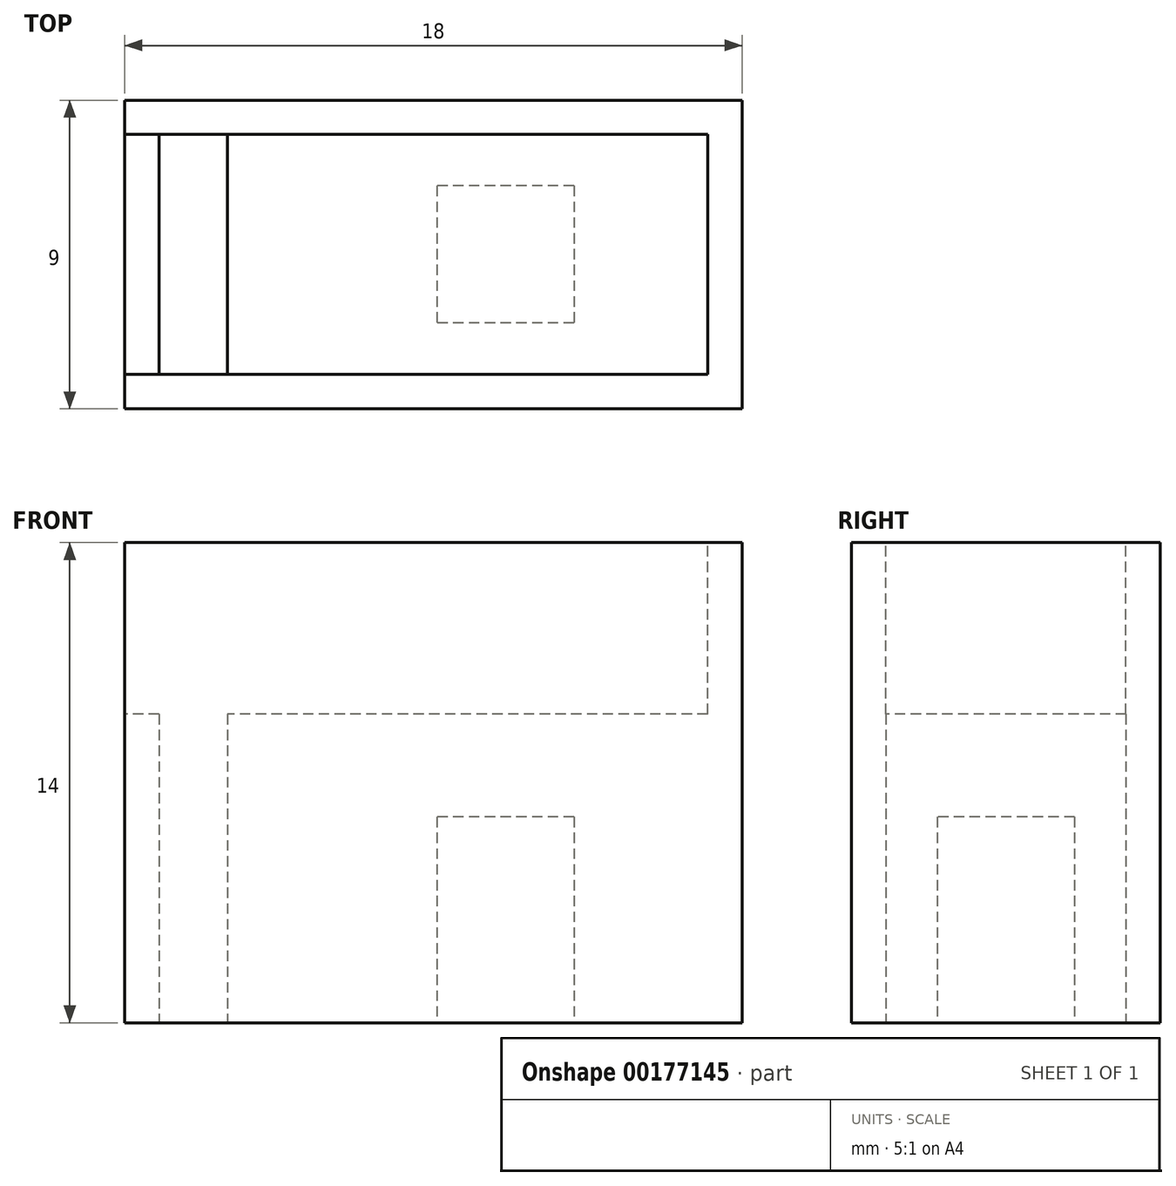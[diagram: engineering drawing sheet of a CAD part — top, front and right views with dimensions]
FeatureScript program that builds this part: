
annotation { "Feature Type Name" : "Feature", "Feature Type Description" : "" }
export const myFeature = defineFeature(function(context is Context, id is Id, definition is map)
    precondition{}
    {
        {
            var Q0;
            Q0=qCreatedBy(makeId("Top.planeOp"),FACE);
            var sketch = newSketch(context, id + "F0", { "sketchPlane" : qUnion([Q0])});
            skLineSegment(sketch, "E0.bottom", {"start": v(9, -4.5) * mm, "end": v(-9, -4.5) * mm});
            skLineSegment(sketch, "E0.top", {"start": v(9, 4.5) * mm, "end": v(-9, 4.5) * mm});
            skLineSegment(sketch, "E0.left", {"start": v(9, -4.5) * mm, "end": v(9, 4.5) * mm});
            skLineSegment(sketch, "E0.right", {"start": v(-9, -4.5) * mm, "end": v(-9, 4.5) * mm});
            skPoint(sketch, "E0.middle", {"position": v(0, 0) * mm});
            skSolve(sketch);
        }
        {
            var Q0;
            Q0=qSketchRegion(id+"F0",true);
            extrude(context, id + "F1", {"entities" : qUnion([Q0]), "depth" : 13 * mm});
        }
        {
            var Q0;
            Q0=makeQuery(id+"F1.opExtrude","CAP_FACE",FACE,{"disambiguationData":[OSD([sQuery(id+"F0.wireOp",EDGE,"E0.bottom"),sQuery(id+"F0.wireOp",EDGE,"E0.top"),sQuery(id+"F0.wireOp",EDGE,"E0.left"),sQuery(id+"F0.wireOp",EDGE,"E0.right")])],"isStart":false});
            var sketch = newSketch(context, id + "F2", { "sketchPlane" : qUnion([Q0])});
            skLineSegment(sketch, "E1.bottom", {"start": v(8, -3.5) * mm, "end": v(-9, -3.5) * mm});
            skLineSegment(sketch, "E1.top", {"start": v(8, 3.5) * mm, "end": v(-9, 3.5) * mm});
            skLineSegment(sketch, "E1.left", {"start": v(8, -3.5) * mm, "end": v(8, 3.5) * mm});
            skLineSegment(sketch, "E1.right", {"start": v(-9, -3.5) * mm, "end": v(-9, 3.5) * mm});
            skPoint(sketch, "E1.middle", {"position": v(-0.5, 0) * mm});
            skSolve(sketch);
        }
        {
            var Q0;
            Q0=qSketchRegion(id+"F2",true);
            extrude(context, id + "F3", {"entities" : qUnion([Q0]), "operationType" : NewBodyOperationType.REMOVE, "oppositeDirection" : true, "depth" : 4 * mm});
        }
        {
            var Q0;
            Q0=makeQuery(id+"F1.opExtrude","CAP_FACE",FACE,{"disambiguationData":[OSD([sQuery(id+"F0.wireOp",EDGE,"E0.bottom"),sQuery(id+"F0.wireOp",EDGE,"E0.top"),sQuery(id+"F0.wireOp",EDGE,"E0.left"),sQuery(id+"F0.wireOp",EDGE,"E0.right")])],"isStart":true});
            var sketch = newSketch(context, id + "F4", { "sketchPlane" : qUnion([Q0])});
            skLineSegment(sketch, "E2.bottom", {"start": v(4.1, -2) * mm, "end": v(0.1, -2) * mm});
            skLineSegment(sketch, "E2.top", {"start": v(4.1, 2) * mm, "end": v(0.1, 2) * mm});
            skLineSegment(sketch, "E2.left", {"start": v(4.1, -2) * mm, "end": v(4.1, 2) * mm});
            skLineSegment(sketch, "E2.right", {"start": v(0.1, -2) * mm, "end": v(0.1, 2) * mm});
            skPoint(sketch, "E2.middle", {"position": v(2.1, 0) * mm});
            skLineSegment(sketch, "E3.bottom", {"start": v(-6, -3.5) * mm, "end": v(-8, -3.5) * mm});
            skLineSegment(sketch, "E3.top", {"start": v(-6, 3.5) * mm, "end": v(-8, 3.5) * mm});
            skLineSegment(sketch, "E3.left", {"start": v(-6, -3.5) * mm, "end": v(-6, 3.5) * mm});
            skLineSegment(sketch, "E3.right", {"start": v(-8, -3.5) * mm, "end": v(-8, 3.5) * mm});
            skPoint(sketch, "E3.middle", {"position": v(-7, 0) * mm});
            skSolve(sketch);
        }
        {
            var Q0;
            Q0=makeQuery(id+"F4.imprint","IMPRINT",FACE,{"disambiguationData":[TD([[makeQuery(id+"F4.imprint","IMPRINT",EDGE,{"derivedFrom":sQuery(id+"F4.wireOp",EDGE,"E2.bottom")}),-1.0]])]});
            extrude(context, id + "F5", {"entities" : qUnion([Q0]), "operationType" : NewBodyOperationType.REMOVE, "oppositeDirection" : true, "depth" : 6 * mm});
        }
        {
            var Q0;
            Q0=makeQuery(id+"F4.imprint","IMPRINT",FACE,{"disambiguationData":[TD([[makeQuery(id+"F4.imprint","IMPRINT",EDGE,{"derivedFrom":sQuery(id+"F4.wireOp",EDGE,"E3.bottom")}),-1.0]])]});
            extrude(context, id + "F6", {"entities" : qUnion([Q0]), "operationType" : NewBodyOperationType.REMOVE, "oppositeDirection" : true, "depth" : 9 * mm});
        }
        {
            var Q0;
            Q0=makeQuery(id+"F1.opExtrude","CAP_FACE",FACE,{"disambiguationData":[OSD([sQuery(id+"F0.wireOp",EDGE,"E0.bottom"),sQuery(id+"F0.wireOp",EDGE,"E0.top"),sQuery(id+"F0.wireOp",EDGE,"E0.left"),sQuery(id+"F0.wireOp",EDGE,"E0.right")])],"isStart":false});
            var sketch = newSketch(context, id + "F7", { "sketchPlane" : qUnion([Q0])});
            skLineSegment(sketch, "E4", {"start": v(-9, 4.5) * mm, "end": v(9, 4.5) * mm});
            skLineSegment(sketch, "E5", {"start": v(9, 4.5) * mm, "end": v(9, -4.5) * mm});
            skLineSegment(sketch, "E6", {"start": v(9, -4.5) * mm, "end": v(-9, -4.5) * mm});
            skLineSegment(sketch, "E7", {"start": v(-9, -4.5) * mm, "end": v(-9, -3.5) * mm});
            skLineSegment(sketch, "E8", {"start": v(-9, -3.5) * mm, "end": v(8, -3.5) * mm});
            skLineSegment(sketch, "E9", {"start": v(8, -3.5) * mm, "end": v(8, 3.5) * mm});
            skLineSegment(sketch, "E10", {"start": v(8, 3.5) * mm, "end": v(-9, 3.5) * mm});
            skLineSegment(sketch, "E11", {"start": v(-9, 3.5) * mm, "end": v(-9, 4.5) * mm});
            skSolve(sketch);
        }
        {
            var Q0;
            Q0=qSketchRegion(id+"F7",true);
            extrude(context, id + "F8", {"entities" : qUnion([Q0]), "operationType" : NewBodyOperationType.ADD, "depth" : 1 * mm});
        }
    });
